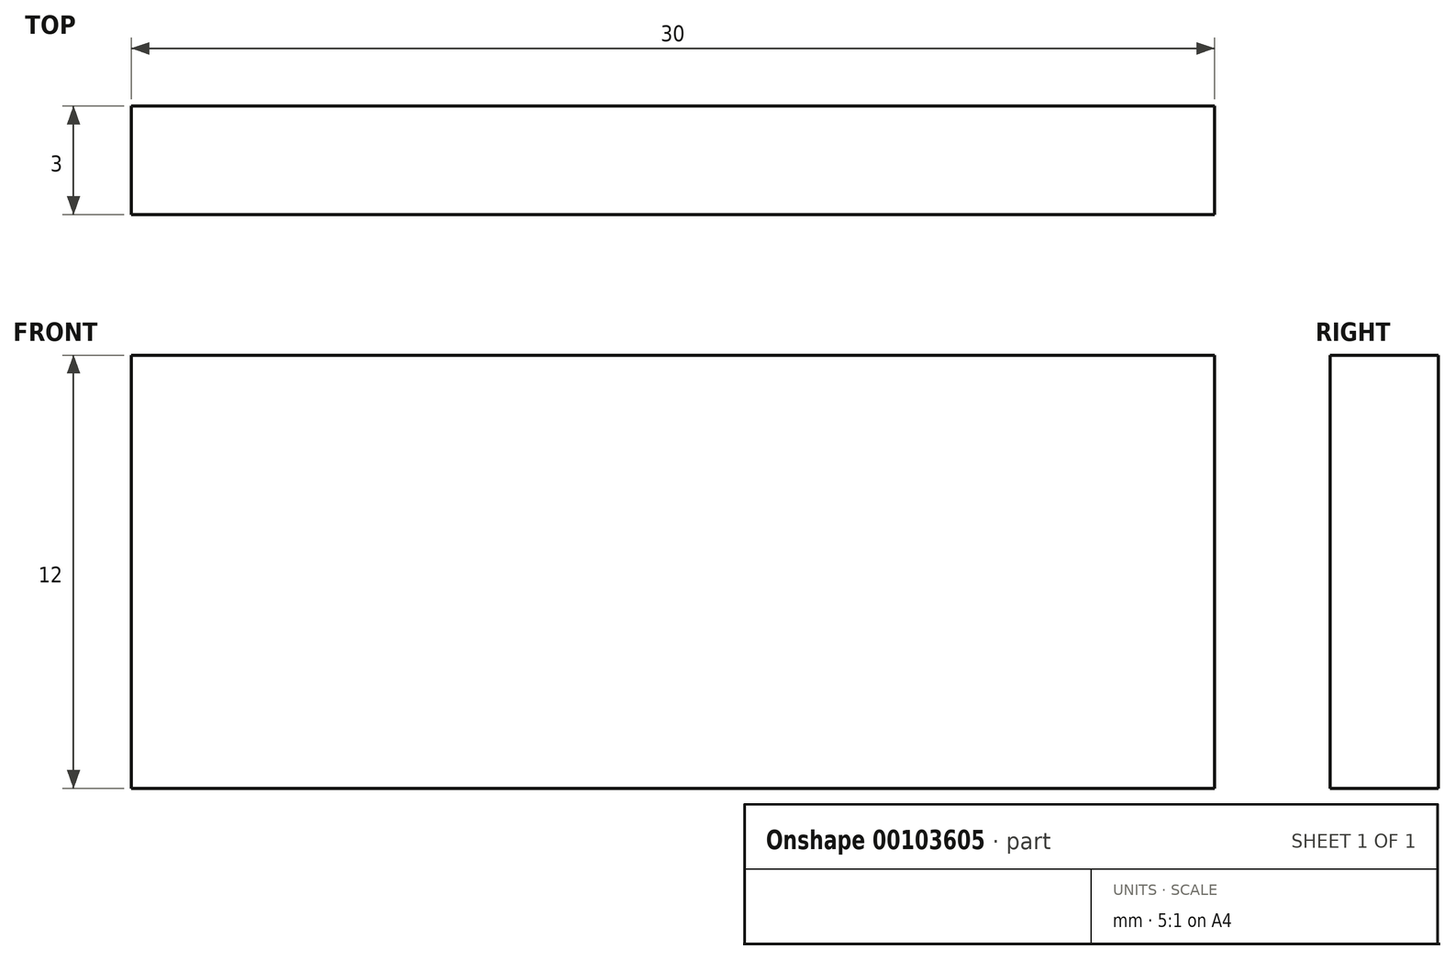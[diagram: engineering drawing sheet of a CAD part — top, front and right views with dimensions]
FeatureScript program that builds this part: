
annotation { "Feature Type Name" : "Feature", "Feature Type Description" : "" }
export const myFeature = defineFeature(function(context is Context, id is Id, definition is map)
    precondition{}
    {
        {
            var Q0;
            Q0=qCreatedBy(makeId("Front.planeOp"),FACE);
            var sketch = newSketch(context, id + "F0", { "sketchPlane" : qUnion([Q0])});
            skLineSegment(sketch, "E0.bottom", {"start": v(-10.92, 9.39) * mm, "end": v(19.08, 9.39) * mm});
            skLineSegment(sketch, "E0.top", {"start": v(-10.92, -2.61) * mm, "end": v(19.08, -2.61) * mm});
            skLineSegment(sketch, "E0.left", {"start": v(-10.92, 9.39) * mm, "end": v(-10.92, -2.61) * mm});
            skLineSegment(sketch, "E0.right", {"start": v(19.08, 9.39) * mm, "end": v(19.08, -2.61) * mm});
            skSolve(sketch);
        }
        {
            var Q0;
            Q0=makeQuery(id+"F0.imprint","IMPRINT",FACE,{"disambiguationData":[TD([[makeQuery(id+"F0.imprint","IMPRINT",EDGE,{"derivedFrom":sQuery(id+"F0.wireOp",EDGE,"E0.bottom")}),-1.0]])]});
            extrude(context, id + "F1", {"entities" : qUnion([Q0]), "depth" : 3 * mm});
        }
    });
